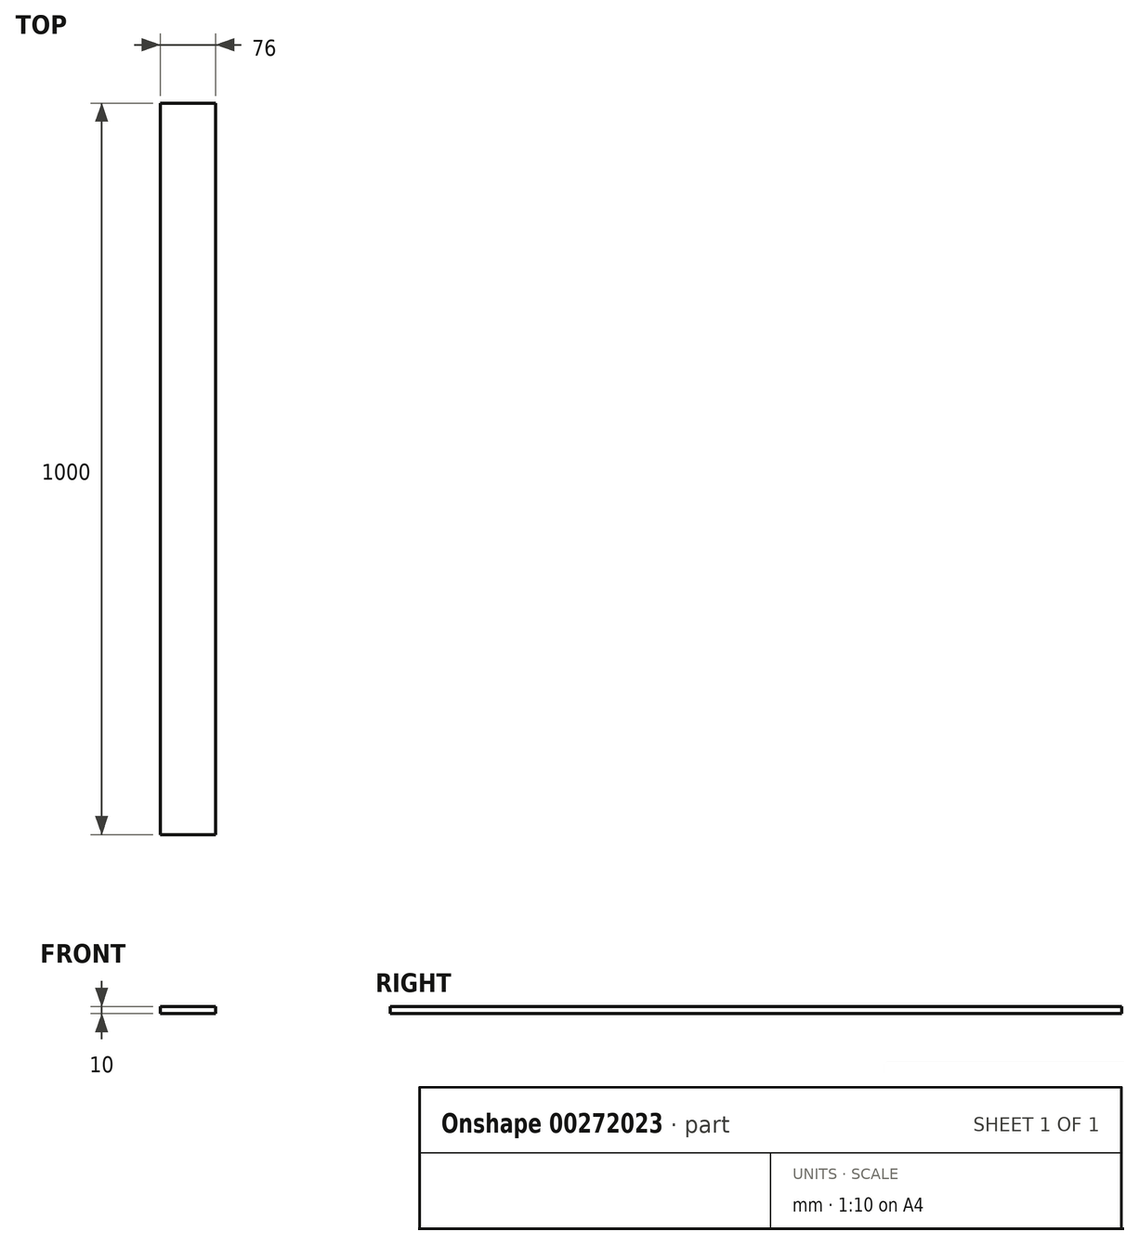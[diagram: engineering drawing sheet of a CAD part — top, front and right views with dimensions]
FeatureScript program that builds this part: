
annotation { "Feature Type Name" : "Feature", "Feature Type Description" : "" }
export const myFeature = defineFeature(function(context is Context, id is Id, definition is map)
    precondition{}
    {
        {
            var Q0;
            Q0=qCreatedBy(makeId("Front.planeOp"),FACE);
            var sketch = newSketch(context, id + "F0", { "sketchPlane" : qUnion([Q0])});
            skLineSegment(sketch, "E0.bottom", {"start": v(38, -5) * mm, "end": v(-38, -5) * mm});
            skLineSegment(sketch, "E0.top", {"start": v(38, 5) * mm, "end": v(-38, 5) * mm});
            skLineSegment(sketch, "E0.left", {"start": v(38, -5) * mm, "end": v(38, 5) * mm});
            skLineSegment(sketch, "E0.right", {"start": v(-38, -5) * mm, "end": v(-38, 5) * mm});
            skPoint(sketch, "E0.middle", {"position": v(0, 0) * mm});
            skSolve(sketch);
        }
        {
            var Q0;
            Q0=makeQuery(id+"F0.imprint","IMPRINT",FACE,{"disambiguationData":[TD([[makeQuery(id+"F0.imprint","IMPRINT",EDGE,{"derivedFrom":sQuery(id+"F0.wireOp",EDGE,"E0.bottom")}),-1.0]])]});
            extrude(context, id + "F1", {"entities" : qUnion([Q0]), "endBound" : BoundingType.SYMMETRIC, "depth" : 1000 * mm});
        }
    });
